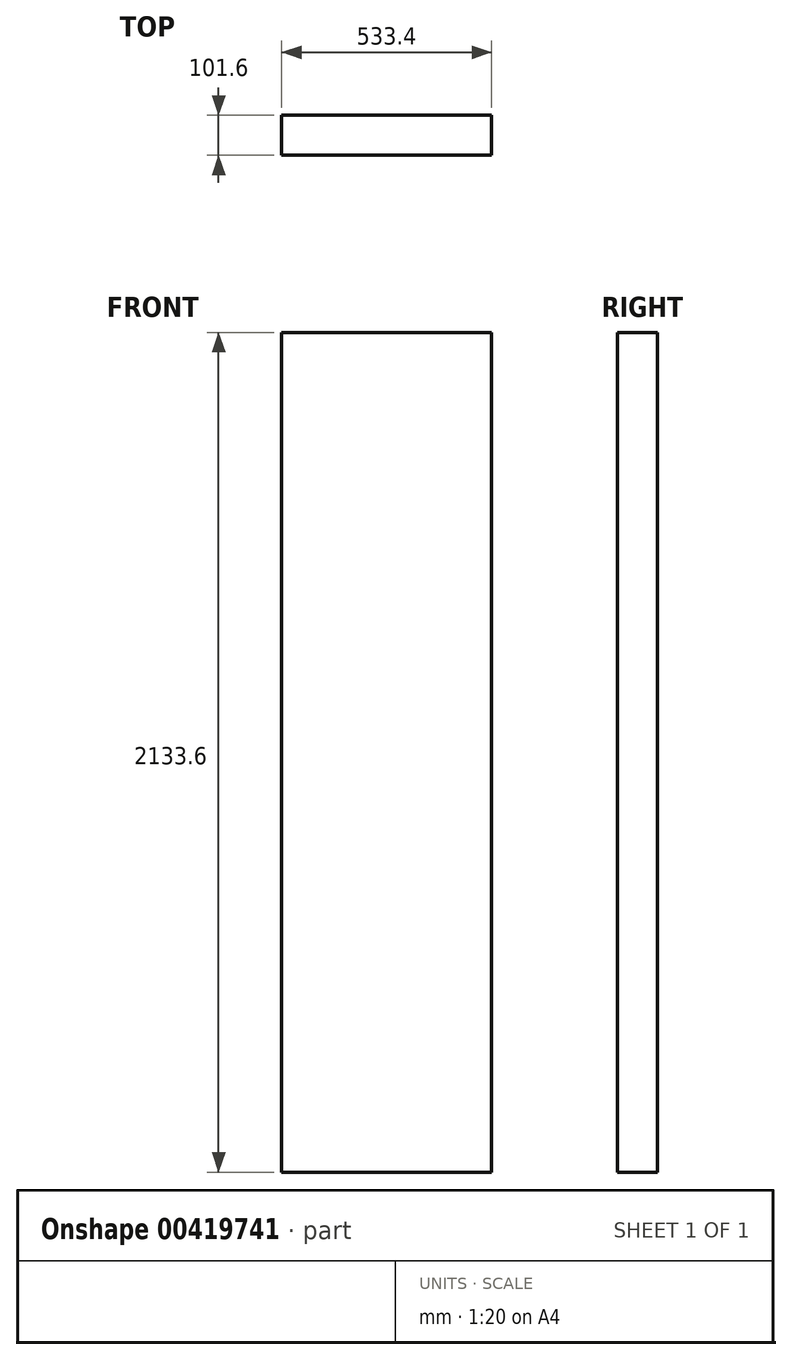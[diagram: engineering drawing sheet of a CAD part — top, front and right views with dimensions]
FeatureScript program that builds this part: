
annotation { "Feature Type Name" : "Feature", "Feature Type Description" : "" }
export const myFeature = defineFeature(function(context is Context, id is Id, definition is map)
    precondition{}
    {
        {
            var Q0;
            Q0=qCreatedBy(makeId("Front.planeOp"),FACE);
            var sketch = newSketch(context, id + "F0", { "sketchPlane" : qUnion([Q0])});
            skLineSegment(sketch, "E0", {"start": v(-354.58, 1022.75) * mm, "end": v(-354.58, -1110.85) * mm});
            skLineSegment(sketch, "E1", {"start": v(-354.58, 1022.75) * mm, "end": v(178.82, 1022.75) * mm});
            skLineSegment(sketch, "E2", {"start": v(178.82, 1022.75) * mm, "end": v(178.82, -1110.85) * mm});
            skLineSegment(sketch, "E3", {"start": v(-354.58, -1110.85) * mm, "end": v(178.82, -1110.85) * mm});
            skSolve(sketch);
        }
        {
            var Q0;
            Q0=makeQuery(id+"F0.imprint","IMPRINT",FACE,{"disambiguationData":[TD([[makeQuery(id+"F0.imprint","IMPRINT",EDGE,{"derivedFrom":sQuery(id+"F0.wireOp",EDGE,"E0")}),1.0]])]});
            extrude(context, id + "F1", {"entities" : qUnion([Q0]), "depth" : 101.6 * mm});
        }
    });
